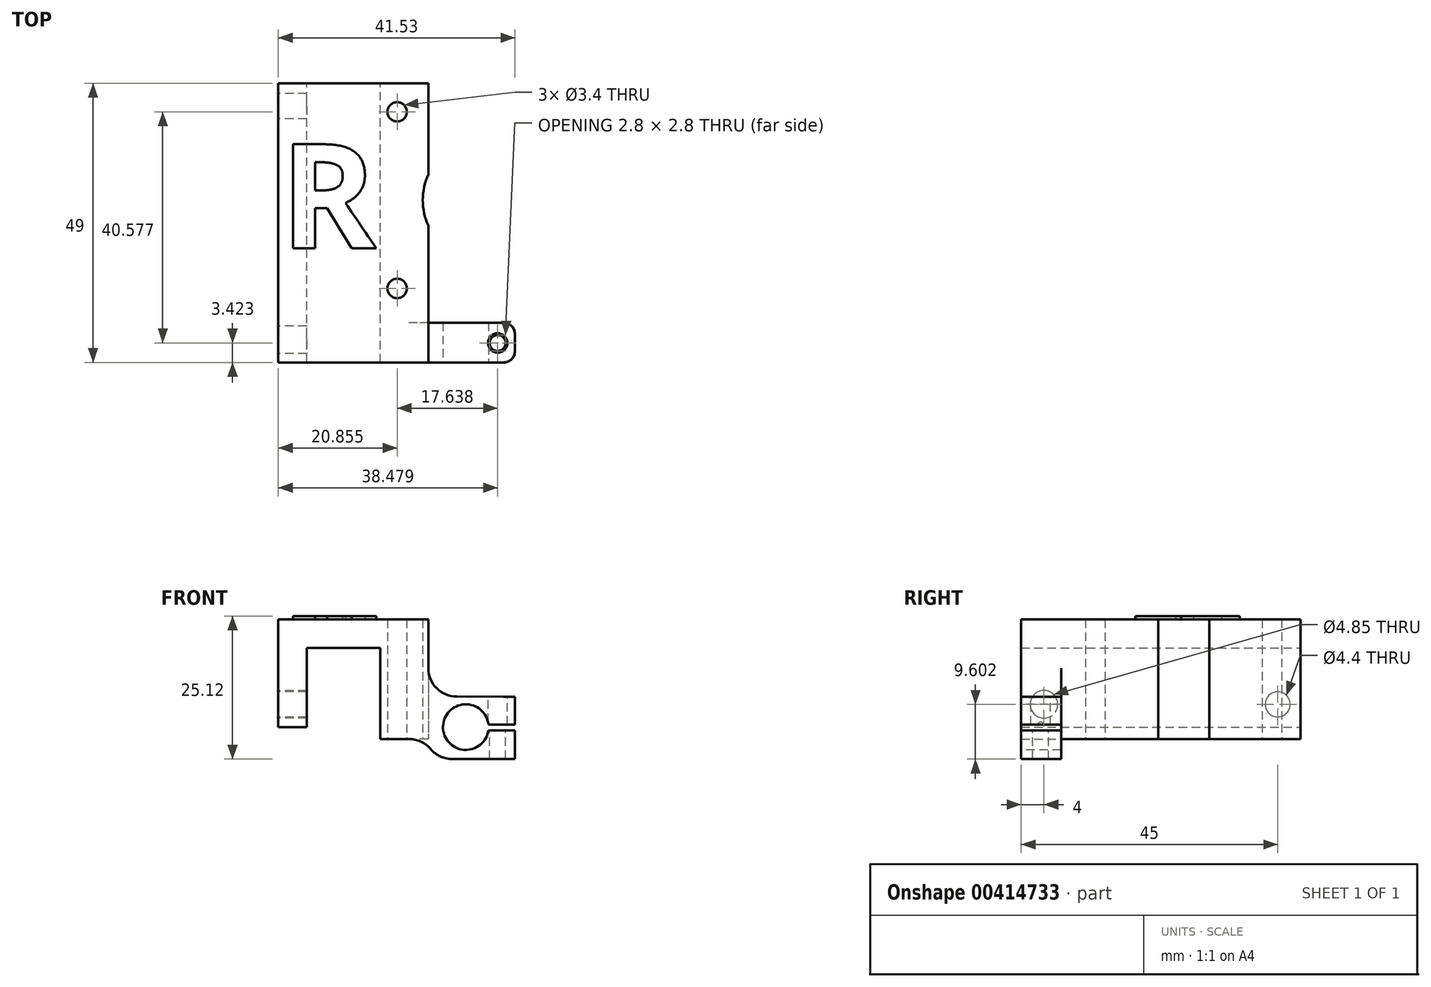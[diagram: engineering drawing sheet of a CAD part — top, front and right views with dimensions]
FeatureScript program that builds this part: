
annotation { "Feature Type Name" : "Feature", "Feature Type Description" : "" }
export const myFeature = defineFeature(function(context is Context, id is Id, definition is map)
    precondition{}
    {
        {
            var Q0;
            Q0=qCreatedBy(makeId("Front.planeOp"),FACE);
            var sketch = newSketch(context, id + "F0", { "sketchPlane" : qUnion([Q0])});
            skLineSegment(sketch, "E0", {"start": v(-18.67, 10.9) * mm, "end": v(-18.67, 29.8) * mm});
            skLineSegment(sketch, "E1", {"start": v(-18.67, 29.8) * mm, "end": v(7.64, 29.8) * mm});
            skLineSegment(sketch, "E2", {"start": v(7.64, 29.8) * mm, "end": v(7.64, 16.27) * mm});
            skLineSegment(sketch, "E3", {"start": v(-0.77, 8.8) * mm, "end": v(-0.77, 24.8) * mm});
            skLineSegment(sketch, "E4", {"start": v(-0.77, 24.8) * mm, "end": v(-13.67, 24.8) * mm});
            skLineSegment(sketch, "E5", {"start": v(-13.67, 24.8) * mm, "end": v(-13.67, 10.9) * mm});
            skLineSegment(sketch, "E6", {"start": v(-13.67, 10.9) * mm, "end": v(-18.67, 10.9) * mm});
            skLineSegment(sketch, "E7", {"start": v(7.64, 16.27) * mm, "end": v(7.64, 8.8) * mm});
            skLineSegment(sketch, "E8", {"start": v(7.64, 8.8) * mm, "end": v(-0.77, 8.8) * mm});
            skLineSegment(sketch, "E9", {"start": v(7.64, 16.27) * mm, "end": v(7.64, 16.27) * mm});
            skLineSegment(sketch, "E10", {"start": v(22.83, 16.24) * mm, "end": v(22.83, 11.34) * mm});
            skLineSegment(sketch, "E11", {"start": v(22.83, 11.34) * mm, "end": v(16.19, 11.34) * mm});
            skLineSegment(sketch, "E12", {"start": v(16.19, 11.34) * mm, "end": v(16.19, 10.34) * mm});
            skLineSegment(sketch, "E13", {"start": v(16.19, 10.34) * mm, "end": v(22.86, 10.34) * mm});
            skLineSegment(sketch, "E14", {"start": v(22.86, 10.34) * mm, "end": v(22.86, 5.29) * mm});
            skLineSegment(sketch, "E15", {"start": v(22.86, 5.29) * mm, "end": v(9.05, 5.29) * mm});
            skLineSegment(sketch, "E16", {"start": v(9.05, 5.29) * mm, "end": v(7.64, 8.8) * mm});
            skLineSegment(sketch, "E17", {"start": v(22.83, 16.24) * mm, "end": v(7.64, 16.27) * mm});
            skSolve(sketch);
        }
        {
            var Q0;
            Q0=makeQuery(id+"F0.imprint","IMPRINT",FACE,{"disambiguationData":[TD([[makeQuery(id+"F0.imprint","IMPRINT",EDGE,{"derivedFrom":sQuery(id+"F0.wireOp",EDGE,"E0")}),-1.0]])]});
            var Q1;
            {var subQ2=sQuery(id+"F0.wireOp",EDGE,"69cbcc5d-e0c3-48db-8baf-3487a8abab7d");Q1=makeQuery(id+"F0.imprint","IMPRINT",FACE,{"disambiguationData":[TD([[makeQuery(id+"F0.imprint","IMPRINT",EDGE,{"derivedFrom":subQ2}),-1.0]])]});}
            var Q2;
            Q2=makeQuery(id+"F0.imprint","IMPRINT",FACE,{"disambiguationData":[TD([[makeQuery(id+"F0.imprint","IMPRINT",EDGE,{"derivedFrom":sQuery(id+"F0.wireOp",EDGE,"E7")}),1.0]])]});
            extrude(context, id + "F1", {"entities" : qUnion([Q0, Q1, Q2]), "depth" : 7 * mm});
        }
        {
            var Q0;
            Q0=makeQuery(id+"F0.imprint","IMPRINT",FACE,{"disambiguationData":[TD([[makeQuery(id+"F0.imprint","IMPRINT",EDGE,{"derivedFrom":sQuery(id+"F0.wireOp",EDGE,"E0")}),-1.0]])]});
            extrude(context, id + "F2", {"entities" : qUnion([Q0]), "operationType" : NewBodyOperationType.ADD, "oppositeDirection" : true, "depth" : 42 * mm});
        }
        {
            var Q0;
            {var subQ0=sQuery(id+"F0.wireOp",EDGE,"E8");Q0=makeQuery(id+"F2.boolean.opBoolean","MERGE",FACE,{"derivedFrom":[makeQuery(id+"F1.opExtrude","SWEPT_FACE",FACE,{"disambiguationData":[OSD([subQ0])]}),makeQuery(id+"F2.opExtrude","SWEPT_FACE",FACE,{"disambiguationData":[OSD([subQ0])]})]});}
            var sketch = newSketch(context, id + "F3", { "sketchPlane" : qUnion([Q0])});
            skCircle(sketch, "E18", {"center": v(2.19, -6) * mm, "radius": 1.7 * mm});
            skCircle(sketch, "E19", {"center": v(2.19, -37) * mm, "radius": 1.7 * mm});
            skCircle(sketch, "E20", {"center": v(17.69, -21.5) * mm, "radius": 11 * mm});
            skSolve(sketch);
        }
        {
            var Q0;
            Q0=qSketchRegion(id+"F3",true);
            extrude(context, id + "F4", {"entities" : qUnion([Q0]), "operationType" : NewBodyOperationType.REMOVE, "endBound" : BoundingType.THROUGH_ALL, "oppositeDirection" : true, "depth" : 25 * mm});
        }
        {
            var Q0;
            Q0=makeQuery(id+"F1.opExtrude","CAP_FACE",FACE,{"disambiguationData":[OSD([sQuery(id+"F0.wireOp",EDGE,"E0"),sQuery(id+"F0.wireOp",EDGE,"E1"),sQuery(id+"F0.wireOp",EDGE,"E2"),sQuery(id+"F0.wireOp",EDGE,"E3"),sQuery(id+"F0.wireOp",EDGE,"E4"),sQuery(id+"F0.wireOp",EDGE,"E5"),sQuery(id+"F0.wireOp",EDGE,"E6"),sQuery(id+"F0.wireOp",EDGE,"E8"),sQuery(id+"F0.wireOp",EDGE,"E9"),sQuery(id+"F0.wireOp",EDGE,"58f11638-63e7-4b32-8aff-a1ba3c53649b"),sQuery(id+"F0.wireOp",EDGE,"E10"),sQuery(id+"F0.wireOp",EDGE,"E11"),sQuery(id+"F0.wireOp",EDGE,"E12"),sQuery(id+"F0.wireOp",EDGE,"E13"),sQuery(id+"F0.wireOp",EDGE,"E14"),sQuery(id+"F0.wireOp",EDGE,"E15"),sQuery(id+"F0.wireOp",EDGE,"E16")])],"isStart":false});
            var sketch = newSketch(context, id + "F5", { "sketchPlane" : qUnion([Q0])});
            skCircle(sketch, "E21", {"center": v(14.23, 10.9) * mm, "radius": 4 * mm});
            skSolve(sketch);
        }
        {
            var Q0;
            Q0=qSketchRegion(id+"F5",true);
            extrude(context, id + "F6", {"entities" : qUnion([Q0]), "operationType" : NewBodyOperationType.REMOVE, "oppositeDirection" : true, "depth" : 10 * mm});
        }
        {
            var Q0;
            Q0=qSketchRegion(id+"F3",true);
            extrude(context, id + "F7", {"entities" : qUnion([Q0]), "operationType" : NewBodyOperationType.REMOVE, "endBound" : BoundingType.THROUGH_ALL, "oppositeDirection" : true, "depth" : 25 * mm});
        }
        {
            var Q0;
            Q0=makeQuery(id+"F1.opExtrude","SWEPT_FACE",FACE,{"disambiguationData":[OSD([sQuery(id+"F0.wireOp",EDGE,"E17")])]});
            var sketch = newSketch(context, id + "F8", { "sketchPlane" : qUnion([Q0])});
            skCircle(sketch, "E22", {"center": v(19.8, -3.58) * mm, "radius": 1.7 * mm});
            skCircle(sketch, "E23", {"center": v(19.8, -3.58) * mm, "radius": 1.4 * mm});
            skSolve(sketch);
        }
        {
            var Q0;
            Q0=makeQuery(id+"F8.imprint","IMPRINT",FACE,{"disambiguationData":[TD([[makeQuery(id+"F8.imprint","IMPRINT",EDGE,{"derivedFrom":sQuery(id+"F8.wireOp",EDGE,"E23")}),1.0]])]});
            extrude(context, id + "F9", {"entities" : qUnion([Q0]), "operationType" : NewBodyOperationType.REMOVE, "endBound" : BoundingType.THROUGH_ALL, "oppositeDirection" : true, "depth" : 25 * mm});
        }
        {
            var Q0;
            Q0=makeQuery(id+"F8.imprint","IMPRINT",FACE,{"disambiguationData":[TD([[makeQuery(id+"F8.imprint","IMPRINT",EDGE,{"derivedFrom":sQuery(id+"F8.wireOp",EDGE,"E22")}),1.0]])]});
            extrude(context, id + "F10", {"entities" : qUnion([Q0]), "operationType" : NewBodyOperationType.REMOVE, "endBound" : BoundingType.UP_TO_NEXT, "oppositeDirection" : true, "depth" : 25 * mm});
        }
        {
            var Q0;
            Q0=makeQuery(id+"F1.opExtrude","SWEPT_EDGE",EDGE,{"disambiguationData":[OSD([sQuery(id+"F0.wireOp",EDGE,"E2"),sQuery(id+"F0.wireOp",EDGE,"E7"),sQuery(id+"F0.wireOp",EDGE,"E17")])]});
            fillet(context, id + "F11", {"entities" : qUnion([Q0]), "radius" : 5 * mm, "tangentPropagation" : true, "allowEdgeOverflow" : false});
        }
        {
            var Q0;
            Q0=makeQuery(id+"F1.opExtrude","SWEPT_EDGE",EDGE,{"disambiguationData":[OSD([sQuery(id+"F0.wireOp",EDGE,"E7"),sQuery(id+"F0.wireOp",EDGE,"E8"),sQuery(id+"F0.wireOp",EDGE,"E16")])]});
            fillet(context, id + "F12", {"entities" : qUnion([Q0]), "radius" : 5 * mm, "tangentPropagation" : true, "allowEdgeOverflow" : false});
        }
        {
            var Q0;
            Q0=makeQuery(id+"F1.opExtrude","SWEPT_EDGE",EDGE,{"disambiguationData":[OSD([sQuery(id+"F0.wireOp",EDGE,"E15"),sQuery(id+"F0.wireOp",EDGE,"E16")])]});
            fillet(context, id + "F13", {"entities" : qUnion([Q0]), "radius" : 5 * mm, "tangentPropagation" : true, "allowEdgeOverflow" : false});
        }
        {
            var Q0;
            Q0=makeQuery(id+"F1.opExtrude","CAP_EDGE",EDGE,{"disambiguationData":[OSD([sQuery(id+"F0.wireOp",EDGE,"E10")])],"isStart":false});
            var Q1;
            Q1=makeQuery(id+"F1.opExtrude","CAP_EDGE",EDGE,{"disambiguationData":[OSD([sQuery(id+"F0.wireOp",EDGE,"E14")])],"isStart":false});
            var Q2;
            Q2=makeQuery(id+"F1.opExtrude","CAP_EDGE",EDGE,{"disambiguationData":[OSD([sQuery(id+"F0.wireOp",EDGE,"E10")])],"isStart":true});
            var Q3;
            Q3=makeQuery(id+"F1.opExtrude","CAP_EDGE",EDGE,{"disambiguationData":[OSD([sQuery(id+"F0.wireOp",EDGE,"E14")])],"isStart":true});
            fillet(context, id + "F14", {"entities" : qUnion([Q0, Q1, Q2, Q3]), "radius" : 2 * mm, "tangentPropagation" : true, "allowEdgeOverflow" : false});
        }
        {
            var Q0;
            {var subQ0=sQuery(id+"F0.wireOp",EDGE,"E0");Q0=makeQuery(id+"F2.boolean.opBoolean","MERGE",FACE,{"derivedFrom":[makeQuery(id+"F1.opExtrude","SWEPT_FACE",FACE,{"disambiguationData":[OSD([subQ0])]}),makeQuery(id+"F2.opExtrude","SWEPT_FACE",FACE,{"disambiguationData":[OSD([subQ0])]})]});}
            var sketch = newSketch(context, id + "F15", { "sketchPlane" : qUnion([Q0])});
            skCircle(sketch, "E24", {"center": v(-38, 14.9) * mm, "radius": 2.2 * mm});
            skCircle(sketch, "E25", {"center": v(3, 14.9) * mm, "radius": 2.43 * mm});
            skSolve(sketch);
        }
        {
            var Q0;
            Q0=qSketchRegion(id+"F15",true);
            extrude(context, id + "F16", {"entities" : qUnion([Q0]), "operationType" : NewBodyOperationType.REMOVE, "oppositeDirection" : true, "depth" : 6 * mm});
        }
        {
            var Q0;
            {var subQ0=sQuery(id+"F0.wireOp",EDGE,"E1");Q0=makeQuery(id+"F2.boolean.opBoolean","MERGE",FACE,{"derivedFrom":[makeQuery(id+"F1.opExtrude","SWEPT_FACE",FACE,{"disambiguationData":[OSD([subQ0])]}),makeQuery(id+"F2.opExtrude","SWEPT_FACE",FACE,{"disambiguationData":[OSD([subQ0])]})]});}
            var sketch = newSketch(context, id + "F17", { "sketchPlane" : qUnion([Q0])});
            skText(sketch, "E26", { "text": "R", "fontName": "OpenSans-Bold.ttf"});
            const initialGuessF17  = {"E26": [-0.01836, 0.01307, 1, 0, 0.0184]};
            skSetInitialGuess(sketch, initialGuessF17);
            skSolve(sketch);
        }
        {
            var Q0;
            Q0 = qSketchRegion(id + "F17", true);
            extrude(context, id + "F18", {"entities" : qUnion([Q0]), "operationType" : NewBodyOperationType.ADD, "depth" : 0.6 * mm});
        }
    });
